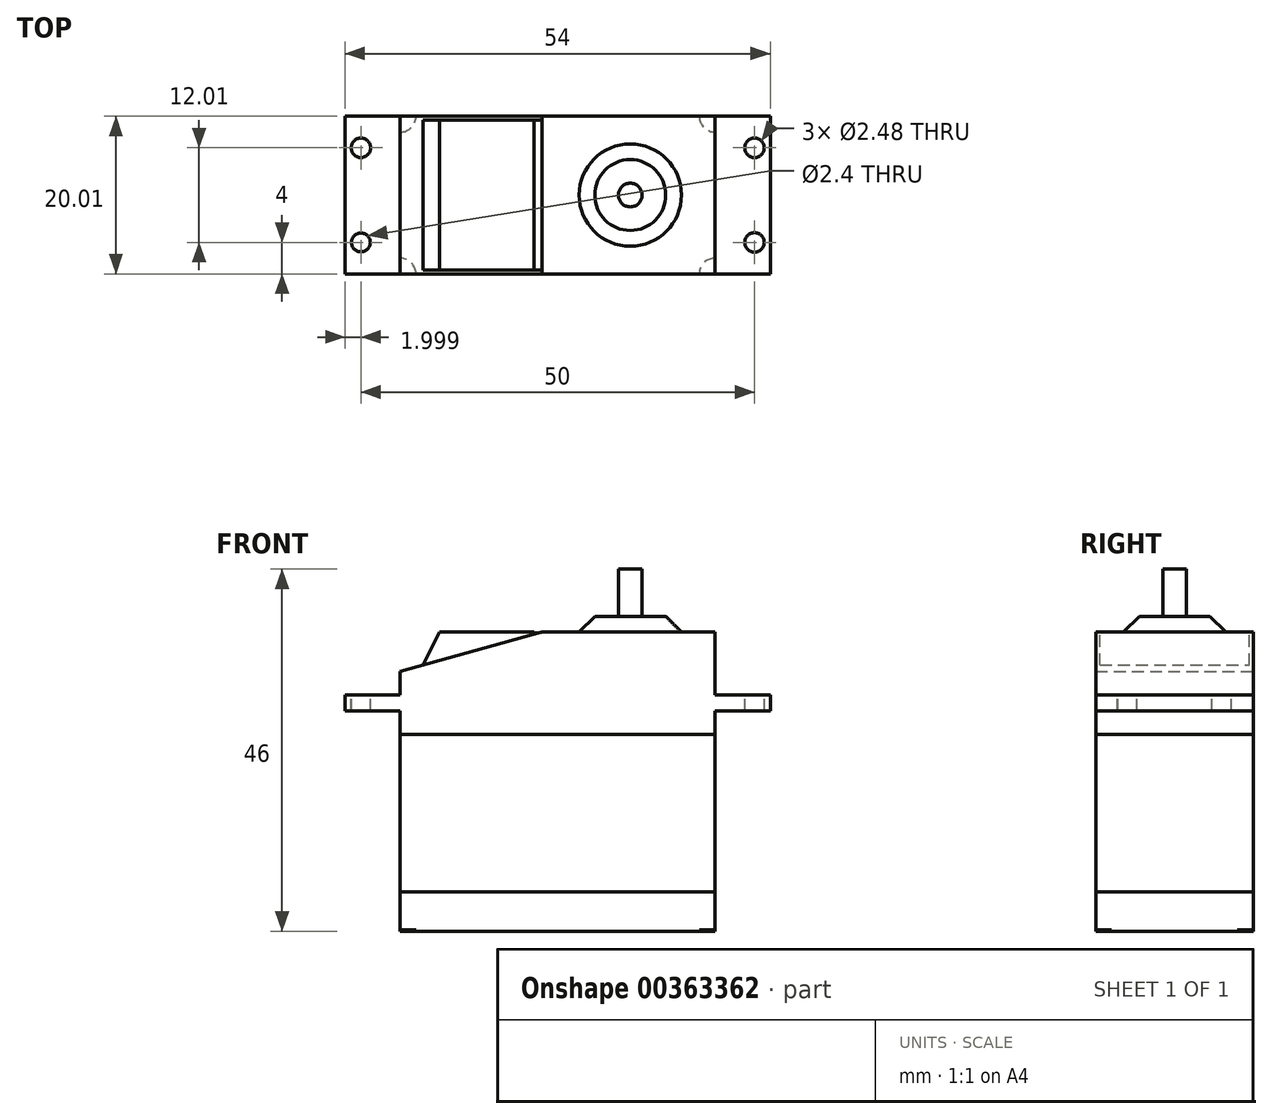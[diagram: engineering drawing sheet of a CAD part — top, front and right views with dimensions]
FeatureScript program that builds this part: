
annotation { "Feature Type Name" : "Feature", "Feature Type Description" : "" }
export const myFeature = defineFeature(function(context is Context, id is Id, definition is map)
    precondition{}
    {
        {
            var Q0;
            Q0=qCreatedBy(makeId("Front.planeOp"),FACE);
            var sketch = newSketch(context, id + "F0", { "sketchPlane" : qUnion([Q0])});
            skLineSegment(sketch, "E0.bottom", {"start": v(-99.42, 8.87) * mm, "end": v(-59.42, 8.87) * mm});
            skLineSegment(sketch, "E0.top", {"start": v(-99.42, -11.13) * mm, "end": v(-59.42, -11.13) * mm});
            skLineSegment(sketch, "E0.left", {"start": v(-99.42, 8.87) * mm, "end": v(-99.42, -11.13) * mm});
            skLineSegment(sketch, "E0.right", {"start": v(-59.42, 8.87) * mm, "end": v(-59.42, -11.13) * mm});
            skLineSegment(sketch, "E1", {"start": v(-99.42, -11.13) * mm, "end": v(-99.42, -16.13) * mm});
            skLineSegment(sketch, "E2", {"start": v(-99.42, -16.13) * mm, "end": v(-59.42, -16.13) * mm});
            skLineSegment(sketch, "E3", {"start": v(-59.42, -16.13) * mm, "end": v(-59.42, -11.13) * mm});
            skLineSegment(sketch, "E4", {"start": v(-99.42, 8.87) * mm, "end": v(-99.42, 16.87) * mm});
            skLineSegment(sketch, "E5", {"start": v(-99.42, 16.87) * mm, "end": v(-81.42, 21.87) * mm});
            skLineSegment(sketch, "E6", {"start": v(-81.42, 21.87) * mm, "end": v(-59.42, 21.87) * mm});
            skLineSegment(sketch, "E7", {"start": v(-59.42, 21.87) * mm, "end": v(-59.42, 8.87) * mm});
            skLineSegment(sketch, "E8", {"start": v(-99.42, 13.87) * mm, "end": v(-106.42, 13.87) * mm});
            skLineSegment(sketch, "E9", {"start": v(-106.42, 13.87) * mm, "end": v(-106.42, 11.87) * mm});
            skLineSegment(sketch, "E10", {"start": v(-106.42, 11.87) * mm, "end": v(-99.42, 11.87) * mm});
            skLineSegment(sketch, "E11", {"start": v(-59.42, 11.87) * mm, "end": v(-52.42, 11.87) * mm});
            skLineSegment(sketch, "E12", {"start": v(-52.42, 11.87) * mm, "end": v(-52.42, 13.87) * mm});
            skLineSegment(sketch, "E13", {"start": v(-52.42, 13.87) * mm, "end": v(-59.42, 13.87) * mm});
            skLineSegment(sketch, "E14", {"start": v(-96.53, 17.67) * mm, "end": v(-94.42, 21.87) * mm});
            skLineSegment(sketch, "E15", {"start": v(-94.42, 21.87) * mm, "end": v(-81.42, 21.87) * mm});
            skSolve(sketch);
        }
        {
            var Q0;
            {var subQ4=sQuery(id+"F0.wireOp",EDGE,"E0.bottom");Q0=makeQuery(id+"F0.imprint","IMPRINT",FACE,{"disambiguationData":[TD([[makeQuery(id+"F0.imprint","IMPRINT",EDGE,{"derivedFrom":subQ4}),1.0]])]});}
            var Q1;
            {var subQ0=sQuery(id+"F0.wireOp",EDGE,"E8");Q1=makeQuery(id+"F0.imprint","IMPRINT",FACE,{"disambiguationData":[TD([[makeQuery(id+"F0.imprint","IMPRINT",EDGE,{"derivedFrom":subQ0}),1.0]])]});}
            var Q2;
            {var subQ0=sQuery(id+"F0.wireOp",EDGE,"E11");Q2=makeQuery(id+"F0.imprint","IMPRINT",FACE,{"disambiguationData":[TD([[makeQuery(id+"F0.imprint","IMPRINT",EDGE,{"derivedFrom":subQ0}),1.0]])]});}
            var Q3;
            Q3=makeQuery(id+"F0.imprint","IMPRINT",FACE,{"disambiguationData":[TD([[makeQuery(id+"F0.imprint","IMPRINT",EDGE,{"derivedFrom":sQuery(id+"F0.wireOp",EDGE,"E0.top")}),-1.0]])]});
            extrude(context, id + "F1", {"entities" : qUnion([Q0, Q1, Q2, Q3]), "depth" : 20.01 * mm});
        }
        {
            var Q0;
            Q0=makeQuery(id+"F0.imprint","IMPRINT",FACE,{"disambiguationData":[TD([[makeQuery(id+"F0.imprint","IMPRINT",EDGE,{"derivedFrom":sQuery(id+"F0.wireOp",EDGE,"E0.bottom")}),-1.0]])]});
            extrude(context, id + "F2", {"entities" : qUnion([Q0]), "depth" : 20 * mm});
        }
        {
            var Q0;
            Q0=makeQuery(id+"F1.opExtrude","SWEPT_FACE",FACE,{"disambiguationData":[OSD([sQuery(id+"F0.wireOp",EDGE,"E8")])]});
            var sketch = newSketch(context, id + "F3", { "sketchPlane" : qUnion([Q0])});
            skCircle(sketch, "E16", {"center": v(-104.42, -4) * mm, "radius": 1.24 * mm});
            skCircle(sketch, "E17", {"center": v(-104.42, -16.01) * mm, "radius": 1.2 * mm});
            skCircle(sketch, "E18", {"center": v(-54.42, -4) * mm, "radius": 1.24 * mm});
            skCircle(sketch, "E19", {"center": v(-54.42, -16.01) * mm, "radius": 1.24 * mm});
            skSolve(sketch);
        }
        {
            var Q0;
            Q0=makeQuery(id+"F3.imprint","IMPRINT",FACE,{"disambiguationData":[TD([[makeQuery(id+"F3.imprint","IMPRINT",EDGE,{"derivedFrom":sQuery(id+"F3.wireOp",EDGE,"E18")}),1.0]])]});
            var Q1;
            Q1=makeQuery(id+"F3.imprint","IMPRINT",FACE,{"disambiguationData":[TD([[makeQuery(id+"F3.imprint","IMPRINT",EDGE,{"derivedFrom":sQuery(id+"F3.wireOp",EDGE,"E19")}),1.0]])]});
            var Q2;
            Q2=makeQuery(id+"F3.imprint","IMPRINT",FACE,{"disambiguationData":[TD([[makeQuery(id+"F3.imprint","IMPRINT",EDGE,{"derivedFrom":sQuery(id+"F3.wireOp",EDGE,"E17")}),1.0]])]});
            var Q3;
            Q3=makeQuery(id+"F3.imprint","IMPRINT",FACE,{"disambiguationData":[TD([[makeQuery(id+"F3.imprint","IMPRINT",EDGE,{"derivedFrom":sQuery(id+"F3.wireOp",EDGE,"E16")}),1.0]])]});
            extrude(context, id + "F4", {"entities" : qUnion([Q0, Q1, Q2, Q3]), "operationType" : NewBodyOperationType.REMOVE, "oppositeDirection" : true, "depth" : 5 * mm});
        }
        {
            var Q0;
            {var subQ2=sQuery(id+"F0.wireOp",EDGE,"E14");Q0=makeQuery(id+"F0.imprint","IMPRINT",FACE,{"disambiguationData":[TD([[makeQuery(id+"F0.imprint","IMPRINT",EDGE,{"derivedFrom":subQ2}),-1.0]])]});}
            extrude(context, id + "F5", {"entities" : qUnion([Q0]), "operationType" : NewBodyOperationType.ADD, "depth" : 19.5 * mm});
        }
        {
            var Q0;
            {var subQ2=sQuery(id+"F0.wireOp",EDGE,"E14");Q0=makeQuery(id+"F0.imprint","IMPRINT",FACE,{"disambiguationData":[TD([[makeQuery(id+"F0.imprint","IMPRINT",EDGE,{"derivedFrom":subQ2}),-1.0]])]});}
            extrude(context, id + "F6", {"entities" : qUnion([Q0]), "operationType" : NewBodyOperationType.REMOVE, "depth" : 0.5 * mm});
        }
        {
            var Q0;
            Q0=makeQuery(id+"F5.boolean.opBoolean","MERGE",FACE,{"derivedFrom":[makeQuery(id+"F1.opExtrude","SWEPT_FACE",FACE,{"disambiguationData":[OSD([sQuery(id+"F0.wireOp",EDGE,"E6")])]}),makeQuery(id+"F5.opExtrude","SWEPT_FACE",FACE,{"disambiguationData":[OSD([sQuery(id+"F0.wireOp",EDGE,"E15")])]})]});
            var sketch = newSketch(context, id + "F7", { "sketchPlane" : qUnion([Q0])});
            skLineSegment(sketch, "E20", {"start": v(-81.42, -0.5) * mm, "end": v(-81.42, -19.5) * mm});
            skLineSegment(sketch, "E21", {"start": v(-81.42, -19.5) * mm, "end": v(-82.42, -19.5) * mm});
            skLineSegment(sketch, "E22", {"start": v(-82.42, -19.5) * mm, "end": v(-82.42, -0.5) * mm});
            skLineSegment(sketch, "E23", {"start": v(-82.42, -0.5) * mm, "end": v(-81.42, -0.5) * mm});
            skCircle(sketch, "E24", {"center": v(-70.2, -10) * mm, "radius": 6.5 * mm});
            skPoint(sketch, "E24.centerSnap0", {"position": v(-81.42, -10) * mm});
            skCircle(sketch, "E25", {"center": v(-70.2, -10) * mm, "radius": 1.5 * mm});
            skSolve(sketch);
        }
        {
            var Q0;
            Q0=makeQuery(id+"F7.imprint","IMPRINT",FACE,{"disambiguationData":[TD([[makeQuery(id+"F7.imprint","IMPRINT",EDGE,{"derivedFrom":sQuery(id+"F7.wireOp",EDGE,"E20")}),-1.0]])]});
            extrude(context, id + "F8", {"entities" : qUnion([Q0]), "operationType" : NewBodyOperationType.REMOVE, "oppositeDirection" : true, "depth" : 0.1 * mm});
        }
        {
            var Q0;
            Q0=makeQuery(id+"F7.imprint","IMPRINT",FACE,{"disambiguationData":[TD([[makeQuery(id+"F7.imprint","IMPRINT",EDGE,{"derivedFrom":sQuery(id+"F7.wireOp",EDGE,"E25")}),1.0]])]});
            extrude(context, id + "F9", {"entities" : qUnion([Q0]), "operationType" : NewBodyOperationType.ADD, "depth" : 8 * mm});
        }
        {
            var Q0;
            Q0=makeQuery(id+"F7.imprint","IMPRINT",FACE,{"disambiguationData":[TD([[makeQuery(id+"F7.imprint","IMPRINT",EDGE,{"derivedFrom":sQuery(id+"F7.wireOp",EDGE,"E24")}),1.0]])]});
            extrude(context, id + "F10", {"entities" : qUnion([Q0]), "operationType" : NewBodyOperationType.ADD, "depth" : 2 * mm});
        }
        {
            var Q0;
            Q0=makeQuery(id+"F10.opExtrude","CAP_EDGE",EDGE,{"disambiguationData":[OSD([sQuery(id+"F7.wireOp",EDGE,"E24")])],"isStart":false});
            chamfer(context, id + "F11", {"entities" : qUnion([Q0]), "width" : 2 * mm, "tangentPropagation" : true});
        }
        {
            var Q0;
            Q0=makeQuery(id+"F1.opExtrude","SWEPT_FACE",FACE,{"disambiguationData":[OSD([sQuery(id+"F0.wireOp",EDGE,"E2")])]});
            var sketch = newSketch(context, id + "F12", { "sketchPlane" : qUnion([Q0])});
            skCircle(sketch, "E26", {"center": v(-59.42, 0) * mm, "radius": 2 * mm});
            skCircle(sketch, "E27", {"center": v(-99.42, 0) * mm, "radius": 2 * mm});
            skCircle(sketch, "E28", {"center": v(-59.42, 20.01) * mm, "radius": 2 * mm});
            skCircle(sketch, "E29", {"center": v(-99.42, 20.01) * mm, "radius": 2 * mm});
            skSolve(sketch);
        }
        {
            var Q0;
            {var subQ0=sQuery(id+"F12.wireOp",EDGE,"E26");var subQ1=sQuery(id+"F0.wireOp",EDGE,"E2");var subQ4=makeQuery(id+"F1.opExtrude","CAP_EDGE",EDGE,{"disambiguationData":[OSD([subQ1])],"isStart":true});var subQ5=makeQuery(id+"F12.imprint","INTERSECT",VERTEX,{"derivedFrom":[subQ4,subQ0]});Q0=makeQuery(id+"F12.imprint","IMPRINT",FACE,{"disambiguationData":[TD([[makeQuery(id+"F12.imprint","IMPRINT",EDGE,{"disambiguationData":[TD([[subQ5,1.0]])],"derivedFrom":subQ0}),1.0]])]});}
            var Q1;
            {var subQ0=sQuery(id+"F12.wireOp",EDGE,"E28");var subQ1=sQuery(id+"F0.wireOp",EDGE,"E2");var subQ4=makeQuery(id+"F1.opExtrude","CAP_EDGE",EDGE,{"disambiguationData":[OSD([subQ1])],"isStart":false});var subQ5=makeQuery(id+"F12.imprint","INTERSECT",VERTEX,{"derivedFrom":[subQ4,subQ0]});Q1=makeQuery(id+"F12.imprint","IMPRINT",FACE,{"disambiguationData":[TD([[makeQuery(id+"F12.imprint","IMPRINT",EDGE,{"disambiguationData":[TD([[subQ5,-1.0]])],"derivedFrom":subQ0}),1.0]])]});}
            var Q2;
            {var subQ0=sQuery(id+"F12.wireOp",EDGE,"E29");var subQ1=sQuery(id+"F0.wireOp",EDGE,"E2");var subQ4=makeQuery(id+"F1.opExtrude","CAP_EDGE",EDGE,{"disambiguationData":[OSD([subQ1])],"isStart":false});var subQ5=makeQuery(id+"F12.imprint","INTERSECT",VERTEX,{"derivedFrom":[subQ4,subQ0]});Q2=makeQuery(id+"F12.imprint","IMPRINT",FACE,{"disambiguationData":[TD([[makeQuery(id+"F12.imprint","IMPRINT",EDGE,{"disambiguationData":[TD([[subQ5,1.0]])],"derivedFrom":subQ0}),1.0]])]});}
            var Q3;
            {var subQ0=sQuery(id+"F12.wireOp",EDGE,"E27");var subQ1=sQuery(id+"F0.wireOp",EDGE,"E2");var subQ4=makeQuery(id+"F1.opExtrude","CAP_EDGE",EDGE,{"disambiguationData":[OSD([subQ1])],"isStart":true});var subQ5=makeQuery(id+"F12.imprint","INTERSECT",VERTEX,{"derivedFrom":[subQ4,subQ0]});Q3=makeQuery(id+"F12.imprint","IMPRINT",FACE,{"disambiguationData":[TD([[makeQuery(id+"F12.imprint","IMPRINT",EDGE,{"disambiguationData":[TD([[subQ5,-1.0]])],"derivedFrom":subQ0}),1.0]])]});}
            extrude(context, id + "F13", {"entities" : qUnion([Q0, Q1, Q2, Q3]), "operationType" : NewBodyOperationType.REMOVE, "oppositeDirection" : true, "depth" : 0.2 * mm});
        }
    });
